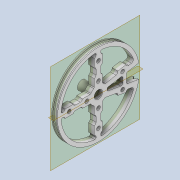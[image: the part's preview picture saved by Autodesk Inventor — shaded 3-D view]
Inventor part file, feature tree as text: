
AUTODESK INVENTOR PART (.ipt)
format: ipt  version: 2020 (Build 240168000, 168)  size: 719,872 bytes
history: native  units: mm
features: sketch x12, extrude x11, projected_geometry x8, fillet x7, plane x2, mirror x2, chamfer x2, thicken_offset x1, revolve x1
ambient origin geometry x8: Origin, YZ Plane, XZ Plane, XY Plane, X Axis, Y Axis, Z Axis, Center Point
bodies: Solid1 (feature_tree)
feature tree (46):
  extrude  "Extrusion1"  Depth=3.0mm
  extrude  "Extrusion2"  Depth=7.0mm
  extrude  "Extrusion3"  Depth=7.0mm
  extrude  "Extrusion4"  Depth=7.0mm
  extrude  "Extrusion5"  Depth=7.0mm
  plane  "Work Plane1"
  mirror  "Mirror1"
  extrude  "Extrusion6"  Depth=7.0mm
  extrude  "Extrusion7"  Depth=7.0mm
  extrude  "Extrusion8"  Depth=4.0mm
  thicken_offset  "Thicken1"
  plane  "Work Plane2"
  revolve  "Revolution1"  [1 undecoded]
  extrude  "Extrusion9"  Depth=7.0mm
  mirror  "Mirror2"
  fillet  "Fillet1"  Radius=7.0mm
  extrude  "Extrusion10"  Depth=4.0mm TaperAngle=0.0deg
  fillet  "Fillet2"  Radius=15.0mm
  fillet  "Fillet3"  Radius=4.0mm
  fillet  "Fillet4"  Radius=1.745329mm
  fillet  "Fillet5"  Radius=1.745329mm
  fillet  "Fillet6"  Radius=4.0mm
  fillet  "Fillet7"  Radius=4.0mm
  extrude  "Extrusion11"  Depth=4.0mm TaperAngle=0.0deg
  chamfer  "Chamfer2"  Distance=10.0mm
  chamfer  "Chamfer3"  Distance=6.0mm
  sketch  "Sketch1"  dims[d0=70.0mm d1=3.0mm]
  sketch  "Sketch2"  dims[d2=25.0mm d3=7.0mm]
  sketch  "Sketch3"  dims[d4=25.0mm d5=7.0mm]
  projected_geometry  "Projected Loop1"
  sketch  "Sketch4"  dims[d6=25.0mm d7=7.0mm]
  projected_geometry  "Projected Loop2"
  sketch  "Sketch5"  dims[d8=10.0mm d9=7.0mm]
  projected_geometry  "Projected Loop3"
  sketch  "Sketch6"  dims[d10=10.0mm d11=7.0mm]
  projected_geometry  "Projected Loop4"
  sketch  "Sketch7"  dims[d12=10.0mm d13=7.0mm]
  sketch  "Sketch8"  dims[d14=4.0mm d15=4.0mm]
  projected_geometry  "Projected Loop5"
  sketch  "Sketch9"  dims[d16=4.0mm d17=7.0mm]
  projected_geometry  "Projected Loop6"
  sketch  "Sketch10"  dims[d18=7.0mm d19=7.0mm d20=7.0mm]
  projected_geometry  "Projected Loop7"
  sketch  "Sketch11"  dims[d21=30.0mm d23=180.0deg d25=4.0mm d26=0.0mm d27=15.0mm d28=4.0mm d29=0.0mm d30=1.745329mm d31=1.745329mm d32=4.0mm d33=4.0mm]
  projected_geometry  "Projected Loop8"
  sketch  "Sketch12"  dims[d34=4.0mm d35=0.0mm d36=4.0mm d37=0.0mm d38=10.0mm d39=6.0mm d40=7.0mm d41=4.0mm d42=0.0mm d43=3.5mm d44=3.5mm d45=3.5mm d46=3.2mm d47=3.2mm d48=3.2mm d49=3.2mm d50=3.2mm d51=3.2mm d52=3.2mm d53=3.2mm d54=4.0mm d55=0.0mm d56=3.0mm d57=4.0mm d58=0.0mm d59=2.5mm d60=10.0mm d61=0.0mm d62=1.0mm d63=1.0mm d64=3.0mm d65=2.0mm d66=10.0mm d67=90.0deg d68=1.5mm d69=1.0mm d70=1.0mm d71=10.0mm d72=0.0mm d73=0.5mm d74=3.0mm d75=10.0mm d76=0.0mm d77=2.0mm d78=2.0mm d79=1.0mm d80=1.5mm d81=1.0mm d82=2.0mm d86=6.15mm d87=3.0mm d88=0.0mm d89=0.5mm d90=2.0mm d91=45.0deg d92=1.575mm d93=2.0mm d94=45.0deg]
note: 1 required parameter value undecoded (feature->parameter linkage not recoverable at this tier; creation-order binding heuristic only, values carry confidence <= 0.55)
